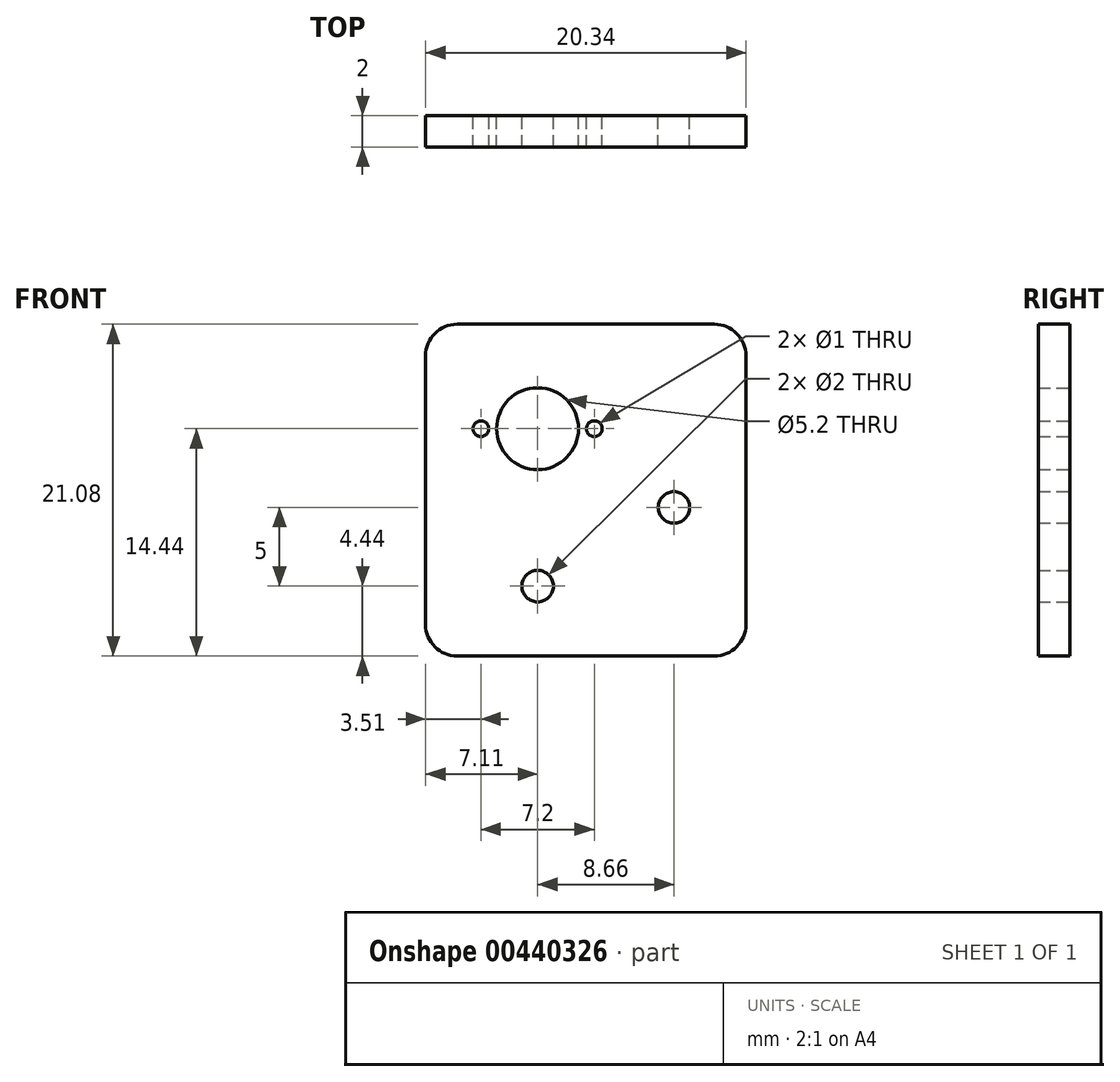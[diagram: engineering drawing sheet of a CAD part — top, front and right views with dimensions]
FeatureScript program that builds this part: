
annotation { "Feature Type Name" : "Feature", "Feature Type Description" : "" }
export const myFeature = defineFeature(function(context is Context, id is Id, definition is map)
    precondition{}
    {
        {
            var Q0;
            Q0=qCreatedBy(makeId("Front.planeOp"),FACE);
            var sketch = newSketch(context, id + "F0", { "sketchPlane" : qUnion([Q0])});
            skLineSegment(sketch, "E0.bottom", {"start": v(-7.11, 6.64) * mm, "end": v(13.23, 6.64) * mm});
            skLineSegment(sketch, "E0.top", {"start": v(-7.11, -14.44) * mm, "end": v(13.23, -14.44) * mm});
            skLineSegment(sketch, "E0.left", {"start": v(-7.11, 6.64) * mm, "end": v(-7.11, -14.44) * mm});
            skLineSegment(sketch, "E0.right", {"start": v(13.23, 6.64) * mm, "end": v(13.23, -14.44) * mm});
            skCircle(sketch, "E1", {"center": v(0, 0) * mm, "radius": 2.6 * mm});
            skLineSegment(sketch, "E2", {"start": v(-3.6, 0) * mm, "end": v(3.6, 0) * mm});
            skCircle(sketch, "E3", {"center": v(-3.6, 0) * mm, "radius": 0.5 * mm});
            skCircle(sketch, "E4", {"center": v(3.6, 0) * mm, "radius": 0.5 * mm});
            skCircle(sketch, "E5", {"center": v(0, -10) * mm, "radius": 1 * mm});
            skCircle(sketch, "E6", {"center": v(8.66, -5) * mm, "radius": 1 * mm});
            skSolve(sketch);
        }
        {
            var Q0;
            Q0 = qSketchRegion(id + "F0", true);
            extrude(context, id + "F1", {"entities" : qUnion([Q0]), "depth" : 2 * mm});
        }
        {
            var Q0;
            Q0=makeQuery(id+"F1.opExtrude","SWEPT_EDGE",EDGE,{"disambiguationData":[OSD([sQuery(id+"F0.wireOp",EDGE,"E0.bottom"),sQuery(id+"F0.wireOp",EDGE,"E0.left")])]});
            var Q1;
            Q1=makeQuery(id+"F1.opExtrude","SWEPT_EDGE",EDGE,{"disambiguationData":[OSD([sQuery(id+"F0.wireOp",EDGE,"E0.bottom"),sQuery(id+"F0.wireOp",EDGE,"E0.right")])]});
            var Q2;
            Q2=makeQuery(id+"F1.opExtrude","SWEPT_EDGE",EDGE,{"disambiguationData":[OSD([sQuery(id+"F0.wireOp",EDGE,"E0.top"),sQuery(id+"F0.wireOp",EDGE,"E0.right")])]});
            var Q3;
            Q3=makeQuery(id+"F1.opExtrude","SWEPT_EDGE",EDGE,{"disambiguationData":[OSD([sQuery(id+"F0.wireOp",EDGE,"E0.top"),sQuery(id+"F0.wireOp",EDGE,"E0.left")])]});
            fillet(context, id + "F2", {"entities" : qUnion([Q0, Q1, Q2, Q3]), "radius" : 2 * mm, "tangentPropagation" : true, "allowEdgeOverflow" : false});
        }
    });
